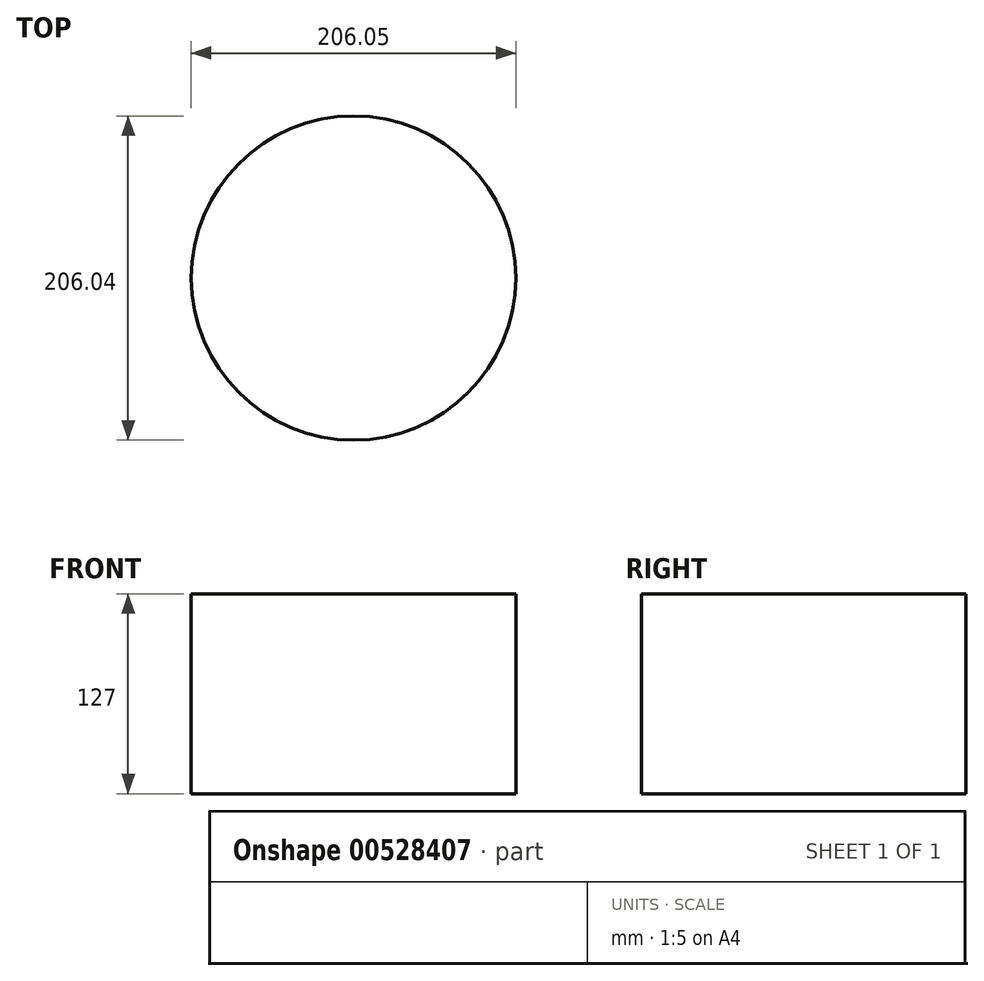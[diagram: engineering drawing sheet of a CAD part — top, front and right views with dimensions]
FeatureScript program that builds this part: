
annotation { "Feature Type Name" : "Feature", "Feature Type Description" : "" }
export const myFeature = defineFeature(function(context is Context, id is Id, definition is map)
    precondition{}
    {
        {
            var Q0;
            Q0=qCreatedBy(makeId("Top.planeOp"),FACE);
            var sketch = newSketch(context, id + "F0", { "sketchPlane" : qUnion([Q0])});
            skCircle(sketch, "E0", {"center": v(-168.13, -34.74) * mm, "radius": 103.02 * mm});
            skSolve(sketch);
        }
        {
            var Q0;
            Q0 = qSketchRegion(id + "F0", true);
            extrude(context, id + "F1", {"entities" : qUnion([Q0]), "depth" : 127 * mm, "offsetDistance" : 25.4 * mm});
        }
    });
